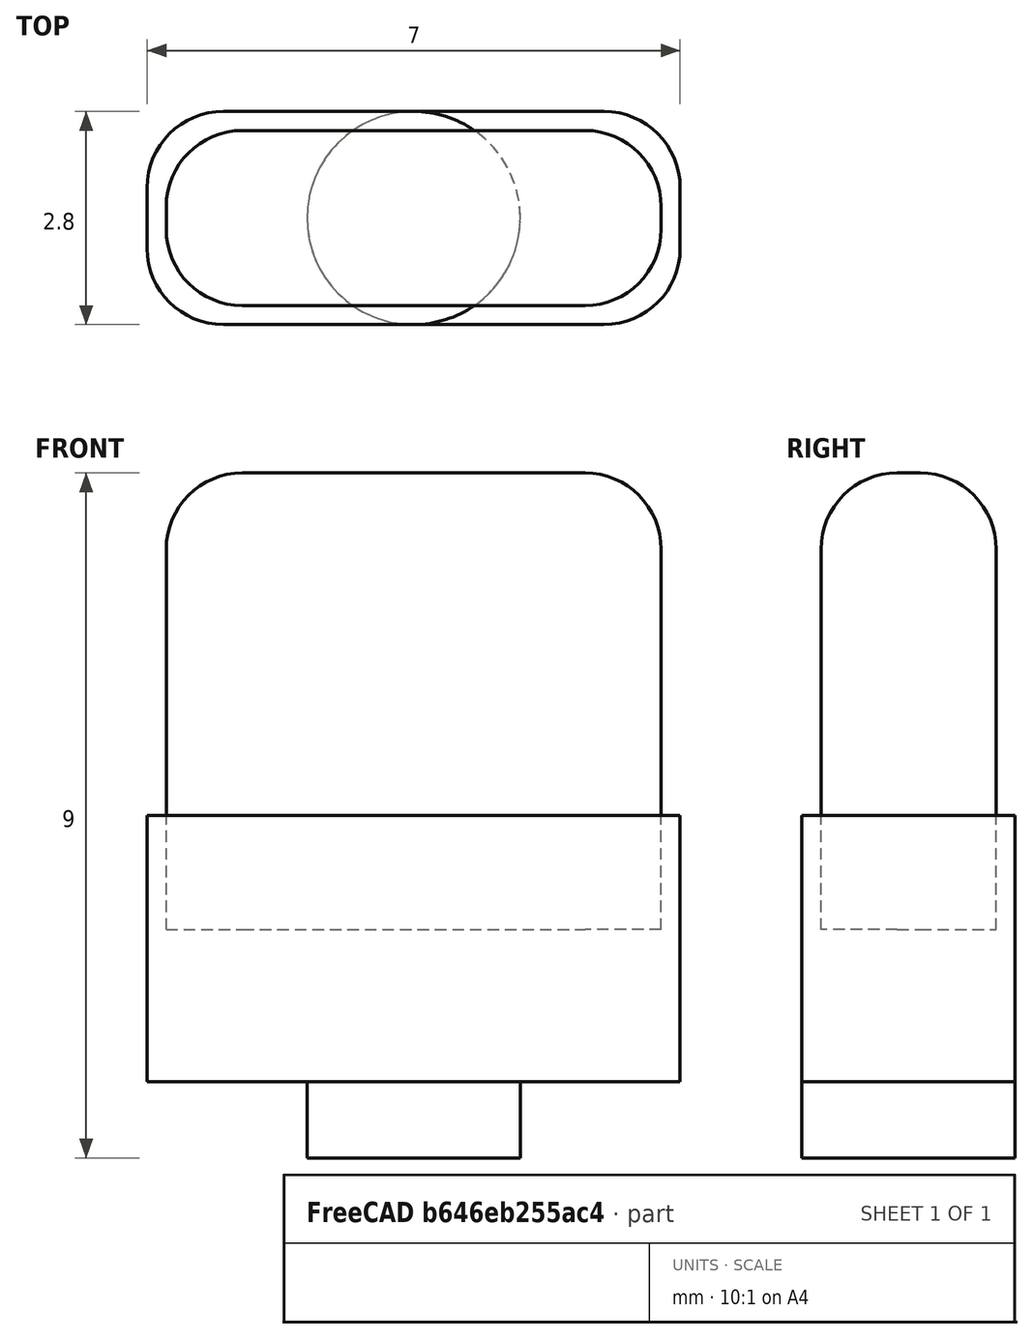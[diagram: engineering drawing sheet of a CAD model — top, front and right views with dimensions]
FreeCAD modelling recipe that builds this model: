
FCSTD DOCUMENT  (FreeCAD 0.18R16131 (Git))
Label: GBC_dome_start_select
License: All rights reserved
LicenseURL: http://en.wikipedia.org/wiki/All_rights_reserved
objects: Part::Box×2, Part::Fillet×2, Part::Cylinder×1
note: 5 computed .brp shape members not serialized (recipe doc carries the construction recipe); baked Part::Feature solids carry a one-line shape summary decoded from their .brp

FEATURE [Part::Box] Box  label="Cube"
  AttacherType = Attacher::AttachEngine3D
  Height = 6
  Length = 6.5
  Width = 2.3
FEATURE [Part::Fillet] Fillet
  Base = -> Box
  Edges = 8 edges r=1: [Edge1,Edge2,Edge3,Edge5,Edge6,Edge7,Edge10,Edge12]
FEATURE [Part::Box] Box001  label="Cube001"
  AttacherType = Attacher::AttachEngine3D
  Height = 3.5
  Length = 7
  Placement = pos=(-0.25,-0.25,-2) rot=(0,0,1;0rad)
  Width = 2.8
FEATURE [Part::Fillet] Fillet001
  Base = -> Box001
  Edges = 4 edges r=1: [Edge1,Edge3,Edge5,Edge7]
FEATURE [Part::Cylinder] Cylinder
  Angle = 360
  AttacherType = Attacher::AttachEngine3D
  Height = 1
  Placement = pos=(3.25,1.15,-3) rot=(0,0,1;0rad)
  Radius = 1.4
